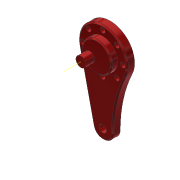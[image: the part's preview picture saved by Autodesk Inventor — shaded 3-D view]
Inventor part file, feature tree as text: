
AUTODESK INVENTOR PART (.ipt)
format: ipt  version: 2019.4 (Build 234330000, 330)  size: 174,080 bytes
history: native  units: mm
features: sketch x4, extrude x4, other x2, hole x2, chamfer x1
ambient origin geometry x8: Origin, YZ Plane, XZ Plane, XY Plane, X Axis, Y Axis, Z Axis, Center Point
bodies: Body1 (feature_tree)
feature tree (13):
  other  "ソリッド1"
  sketch  "スケッチ1"
  extrude  "押し出し1"  Depth=3.0mm
  extrude  "押し出し4"  Depth=26.0mm
  hole  "穴1"  [1 undecoded]
  hole  "穴2"  [1 undecoded]
  extrude  "押し出し2"  Depth=80.0mm TaperAngle=360.0deg
  extrude  "押し出し3"  Depth=3.0mm TaperAngle=0.0deg
  other  "ROLL_OUTPUT_OFFSET"
  chamfer  "面取り1"  Distance=8.0mm
  sketch  "スケッチ2"
  sketch  "スケッチ3"
  sketch  "スケッチ5"
note: 2 required parameter values undecoded (feature->parameter linkage not recoverable at this tier; creation-order binding heuristic only, values carry confidence <= 0.55)
